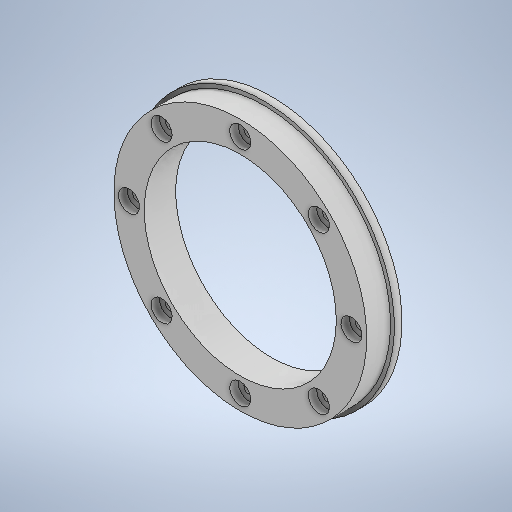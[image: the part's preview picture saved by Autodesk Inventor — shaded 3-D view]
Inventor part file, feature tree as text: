
AUTODESK INVENTOR PART (.ipt)
format: ipt  version: 2025 (Build 290162010, 162A)  size: 333,824 bytes
history: native  units: mm
features: extrude x4, sketch x4, pattern_circular x1, projected_geometry x1
ambient origin geometry x8: Origin, YZ Plane, XZ Plane, XY Plane, X Axis, Y Axis, Z Axis, Center Point
bodies: Solid1 (feature_tree)
feature tree (10):
  extrude  "Extrusion1"  Depth=250.0mm
  extrude  "Extrusion2"  Depth=41.0mm
  extrude  "Extrusion3"  Depth=80.0mm TaperAngle=360.0deg
  pattern_circular  "Circular Pattern1"  [2 undecoded]
  extrude  "Extrusion4"  Depth=10.0mm
  sketch  "Sketch1"  dims[d0=39.5mm d1=250.0mm]
  sketch  "Sketch2"  dims[d2=41.0mm d3=0.0mm d4=12.5mm]
  projected_geometry  "Projected Loop1"
  sketch  "Sketch3"  dims[d5=0.0mm d6=0.0mm d7=80.0mm d8=360.0deg]
  sketch  "Sketch4"  dims[d10=27.5mm d11=11.0mm d12=0.0mm d13=5.0mm d14=10.0mm d15=0.0mm]
note: 2 required parameter values undecoded (feature->parameter linkage not recoverable at this tier; creation-order binding heuristic only, values carry confidence <= 0.55)
